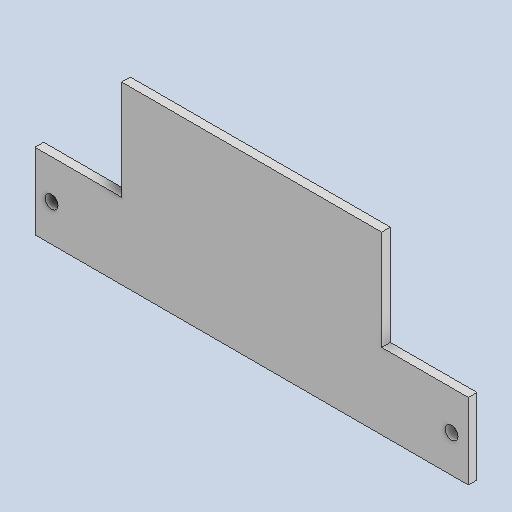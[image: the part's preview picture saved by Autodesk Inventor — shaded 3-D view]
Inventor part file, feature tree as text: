
AUTODESK INVENTOR PART (.ipt)
format: ipt  version: 2023 (Build 270158000, 158)  size: 248,832 bytes
history: native  units: in
note: dims shown in document units (in); Inventor stores cm internally (conversion verified against a paired STEP export)
features: reference x12, other x6, extrude x5, sketch x5, projected_geometry x1
ambient origin geometry x8: Origin, YZ Plane, XZ Plane, XY Plane, X Axis, Y Axis, Z Axis, Center Point
bodies: Body1 (feature_tree)
feature tree (29):
  other  "Bryła1"
  extrude  "Wyciągnięcie proste1"  Depth=0.6496in
  extrude  "Wyciągnięcie proste2"  Depth=0.0787in TaperAngle=0.0deg
  extrude  "Wyciągnięcie proste3"  Depth=0.0787in TaperAngle=0.0deg
  extrude  "Wyciągnięcie proste4"  Depth=0.6693in
  extrude  "Wyciągnięcie proste5"  Depth=0.0787in TaperAngle=0.0deg
  sketch  "Szkic1"
  reference  "Odniesienie1"
  reference  "Odniesienie2"
  reference  "Odniesienie3"
  reference  "Odniesienie4"
  reference  "Odniesienie5"
  reference  "Odniesienie6"
  reference  "Odniesienie7"
  reference  "Odniesienie8"
  reference  "Odniesienie9"
  reference  "Odniesienie10"
  sketch  "Szkic2"
  reference  "Odniesienie11"
  sketch  "Szkic3"
  projected_geometry  "Pętla rzutowana1"
  sketch  "Szkic4"
  reference  "Odniesienie12"
  sketch  "Szkic5"
  other  "<userpath>\Desktop\MojeRoboty\Stefan\mechanics 2\STEFAN.iam"
  other  "STEFAN.iam"
  other  "sciana_awaryjna:1"
  other  "dach:1"
  other  "uchwyt_silnikow:1"
